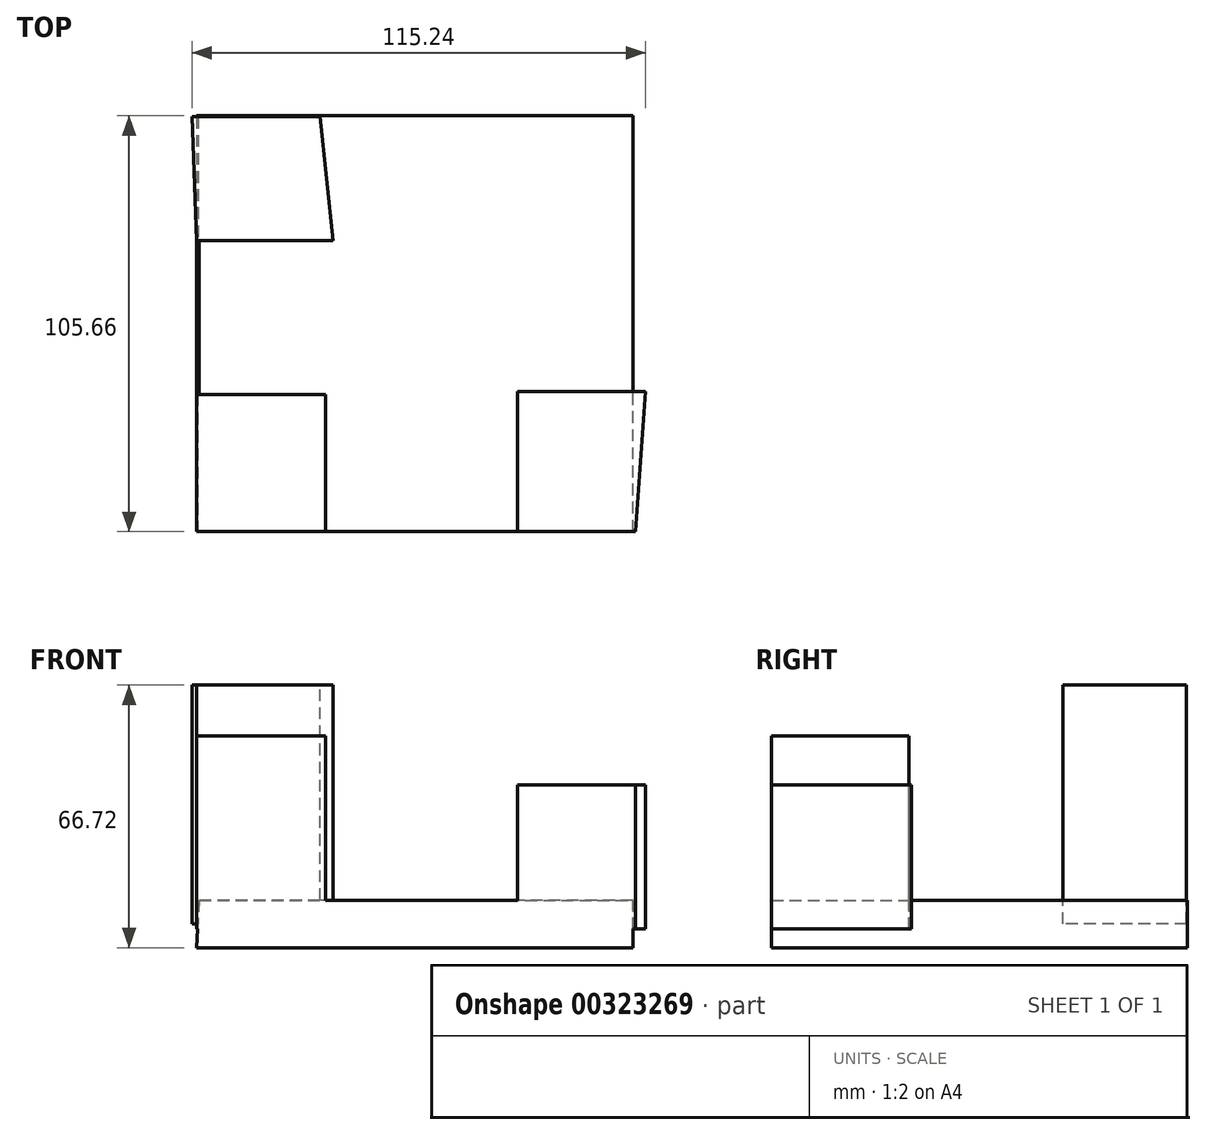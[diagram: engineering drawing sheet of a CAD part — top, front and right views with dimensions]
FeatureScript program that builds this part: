
annotation { "Feature Type Name" : "Feature", "Feature Type Description" : "" }
export const myFeature = defineFeature(function(context is Context, id is Id, definition is map)
    precondition{}
    {
        {
            var Q0;
            Q0=qCreatedBy(makeId("Front.planeOp"),FACE);
            var sketch = newSketch(context, id + "F0", { "sketchPlane" : qUnion([Q0])});
            skLineSegment(sketch, "E0", {"start": v(-55.4, -29.25) * mm, "end": v(54.78, -29.25) * mm});
            skLineSegment(sketch, "E1", {"start": v(54.78, -29.25) * mm, "end": v(54.78, -41.32) * mm});
            skLineSegment(sketch, "E2", {"start": v(54.78, -41.32) * mm, "end": v(-56.02, -41.32) * mm});
            skLineSegment(sketch, "E3", {"start": v(-56.02, -41.32) * mm, "end": v(-55.4, -29.25) * mm});
            skSolve(sketch);
        }
        {
            var Q0;
            Q0=makeQuery(id+"F0.imprint","IMPRINT",FACE,{"disambiguationData":[TD([[makeQuery(id+"F0.imprint","IMPRINT",EDGE,{"derivedFrom":sQuery(id+"F0.wireOp",EDGE,"E0")}),-1.0]])]});
            extrude(context, id + "F1", {"entities" : qUnion([Q0]), "oppositeDirection" : true, "depth" : 105.66 * mm});
        }
        {
            var Q0;
            Q0=qCreatedBy(makeId("Top.planeOp"),FACE);
            var sketch = newSketch(context, id + "F2", { "sketchPlane" : qUnion([Q0])});
            skLineSegment(sketch, "E4", {"start": v(-56.14, 105.4) * mm, "end": v(-23.27, 105.4) * mm});
            skLineSegment(sketch, "E5", {"start": v(-23.27, 105.4) * mm, "end": v(-23.27, 83.99) * mm});
            skLineSegment(sketch, "E6", {"start": v(-23.27, 83.99) * mm, "end": v(-55.77, 83.99) * mm});
            skLineSegment(sketch, "E7", {"start": v(-55.77, 83.99) * mm, "end": v(-56.14, 105.4) * mm});
            skLineSegment(sketch, "E8", {"start": v(24.75, 105.4) * mm, "end": v(53.93, 105.4) * mm});
            skLineSegment(sketch, "E9", {"start": v(53.93, 105.4) * mm, "end": v(53.93, 76.23) * mm});
            skLineSegment(sketch, "E10", {"start": v(53.93, 76.23) * mm, "end": v(23.64, 76.23) * mm});
            skLineSegment(sketch, "E11", {"start": v(23.64, 76.23) * mm, "end": v(24.75, 105.4) * mm});
            skLineSegment(sketch, "E12", {"start": v(-56.14, 34.86) * mm, "end": v(-23.27, 34.86) * mm});
            skLineSegment(sketch, "E13", {"start": v(-23.27, 34.86) * mm, "end": v(-23.27, 0) * mm});
            skLineSegment(sketch, "E14", {"start": v(-23.27, 0) * mm, "end": v(-56.14, 0) * mm});
            skLineSegment(sketch, "E15", {"start": v(-56.14, 0) * mm, "end": v(-56.14, 34.86) * mm});
            skLineSegment(sketch, "E16", {"start": v(25.49, 35.6) * mm, "end": v(57.99, 35.6) * mm});
            skLineSegment(sketch, "E17", {"start": v(25.49, 35.6) * mm, "end": v(25.49, 0) * mm});
            skLineSegment(sketch, "E18", {"start": v(25.49, 0) * mm, "end": v(55.4, 0) * mm});
            skLineSegment(sketch, "E19", {"start": v(55.4, 0) * mm, "end": v(57.99, 35.6) * mm});
            skSolve(sketch);
        }
        {
            var Q0;
            Q0=makeQuery(id+"F2.imprint","IMPRINT",FACE,{"disambiguationData":[TD([[makeQuery(id+"F2.imprint","IMPRINT",EDGE,{"derivedFrom":sQuery(id+"F2.wireOp",EDGE,"E16")}),-1.0]])]});
            var Q1;
            Q1=makeQuery(id+"F2.imprint","IMPRINT",FACE,{"disambiguationData":[TD([[makeQuery(id+"F2.imprint","IMPRINT",EDGE,{"derivedFrom":sQuery(id+"F2.wireOp",EDGE,"E12")}),-1.0]])]});
            extrude(context, id + "F3", {"entities" : qUnion([Q0, Q1]), "operationType" : NewBodyOperationType.ADD, "oppositeDirection" : true, "depth" : 36.58 * mm});
        }
        {
            var Q0;
            Q0=makeQuery(id+"F3.opExtrude","CAP_FACE",FACE,{"disambiguationData":[OSD([sQuery(id+"F2.wireOp",EDGE,"E12"),sQuery(id+"F2.wireOp",EDGE,"E13"),sQuery(id+"F2.wireOp",EDGE,"E14"),sQuery(id+"F2.wireOp",EDGE,"E15")])],"isStart":true});
            extrude(context, id + "F4", {"entities" : qUnion([Q0]), "operationType" : NewBodyOperationType.ADD, "depth" : 12.45 * mm});
        }
        {
            var Q0;
            Q0=qCreatedBy(makeId("Top.planeOp"),FACE);
            var sketch = newSketch(context, id + "F5", { "sketchPlane" : qUnion([Q0])});
            skLineSegment(sketch, "E20", {"start": v(-57.25, 105.4) * mm, "end": v(-24.75, 105.4) * mm});
            skLineSegment(sketch, "E21", {"start": v(-24.75, 105.4) * mm, "end": v(-21.42, 74.01) * mm});
            skLineSegment(sketch, "E22", {"start": v(-21.42, 74.01) * mm, "end": v(-56.14, 74.01) * mm});
            skLineSegment(sketch, "E23", {"start": v(-56.14, 74.01) * mm, "end": v(-57.25, 105.4) * mm});
            skSolve(sketch);
        }
        {
            var Q0;
            Q0=makeQuery(id+"F5.imprint","IMPRINT",FACE,{"disambiguationData":[TD([[makeQuery(id+"F5.imprint","IMPRINT",EDGE,{"derivedFrom":sQuery(id+"F5.wireOp",EDGE,"E20")}),-1.0]])]});
            extrude(context, id + "F6", {"entities" : qUnion([Q0]), "operationType" : NewBodyOperationType.ADD, "oppositeDirection" : true, "depth" : 35.3 * mm});
        }
        {
            var Q0;
            Q0=makeQuery(id+"F6.opExtrude","CAP_FACE",FACE,{"disambiguationData":[OSD([sQuery(id+"F5.wireOp",EDGE,"E20"),sQuery(id+"F5.wireOp",EDGE,"E21"),sQuery(id+"F5.wireOp",EDGE,"E22"),sQuery(id+"F5.wireOp",EDGE,"E23")])],"isStart":true});
            extrude(context, id + "F7", {"entities" : qUnion([Q0]), "operationType" : NewBodyOperationType.ADD, "depth" : 25.4 * mm});
        }
    });
